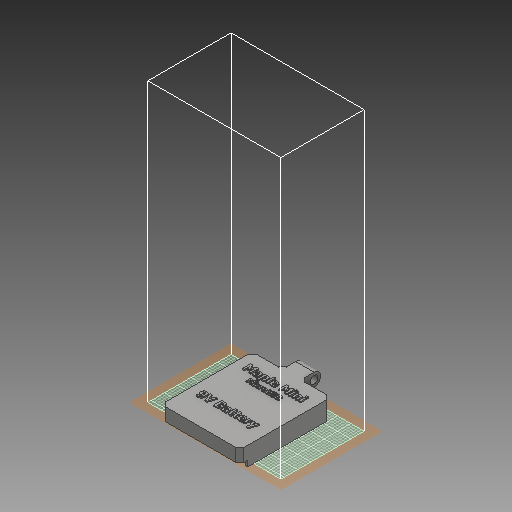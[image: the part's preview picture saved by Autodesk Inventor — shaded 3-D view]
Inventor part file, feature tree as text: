
AUTODESK INVENTOR PART (.ipt)
format: ipt  version: 2018 (Build 220112000, 112)  size: 1,209,344 bytes
history: native  units: in
note: dims shown in document units (in); Inventor stores cm internally (conversion verified against a paired STEP export)
features: extrude x3, sketch x3, move_body x2, chamfer x1, fillet x1, direct_edit x1, plane x1
ambient origin geometry x8: Origin, YZ Plane, XZ Plane, XY Plane, X Axis, Y Axis, Z Axis, Center Point
bodies: Solid1 (feature_tree)
feature tree (12):
  extrude  "Extrusion1"  Depth=0.35in
  chamfer  "Chamfer1"  Distance=1.723in
  fillet  "Fillet1"  Radius=0.246in
  extrude  "Extrusion2"  Depth=0.11in TaperAngle=45.0deg
  extrude  "Extrusion3"  Depth=0.123in
  direct_edit  "Direct Edit1"
  plane  "Work Plane1"
  sketch  "Sketch1"  dims[d0=0.35in d1=0.375in]
  sketch  "Sketch2"  dims[d2=0.57in]
  sketch  "Sketch4"  dims[d3=0.57in d4=1.723in d5=0.246in d6=0.0in d7=0.075in d8=0.125in d9=45.0deg d10=0.123in d11=0.146in d12=0.246in d13=0.0in d16=0.05in d17=0.125in d19=0.11in d20=0.0in d21=0.0in d22=0.0in d23=0.105in d24=0.0in d25=0.0in d26=0.105in]
  move_body  "Move1"
  move_body  "Move2"
